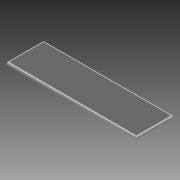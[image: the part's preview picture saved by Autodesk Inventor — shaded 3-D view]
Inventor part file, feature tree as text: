
AUTODESK INVENTOR PART (.ipt)
format: ipt  version: 2013 (Build 170138000, 138)  size: 87,040 bytes
history: native  units: mm
features: extrude x2, sketch x2, other x1
ambient origin geometry x8: Origin, YZ Plane, XZ Plane, XY Plane, X Axis, Y Axis, Z Axis, Center Point
bodies: Volumenkörper1 (feature_tree)
feature tree (5):
  extrude  "Extrusion1"  Depth=18.5mm
  extrude  "Extrusion2"  Depth=63.6mm
  sketch  "Skizze1"  dims[d0=65.0mm d2=18.5mm]
  sketch  "Skizze2"  dims[d3=1.0mm d4=0.0mm d5=63.6mm d7=17.1mm d8=0.7mm d9=0.7mm d10=0.3mm d11=0.0mm]
  other  "Bild1"
